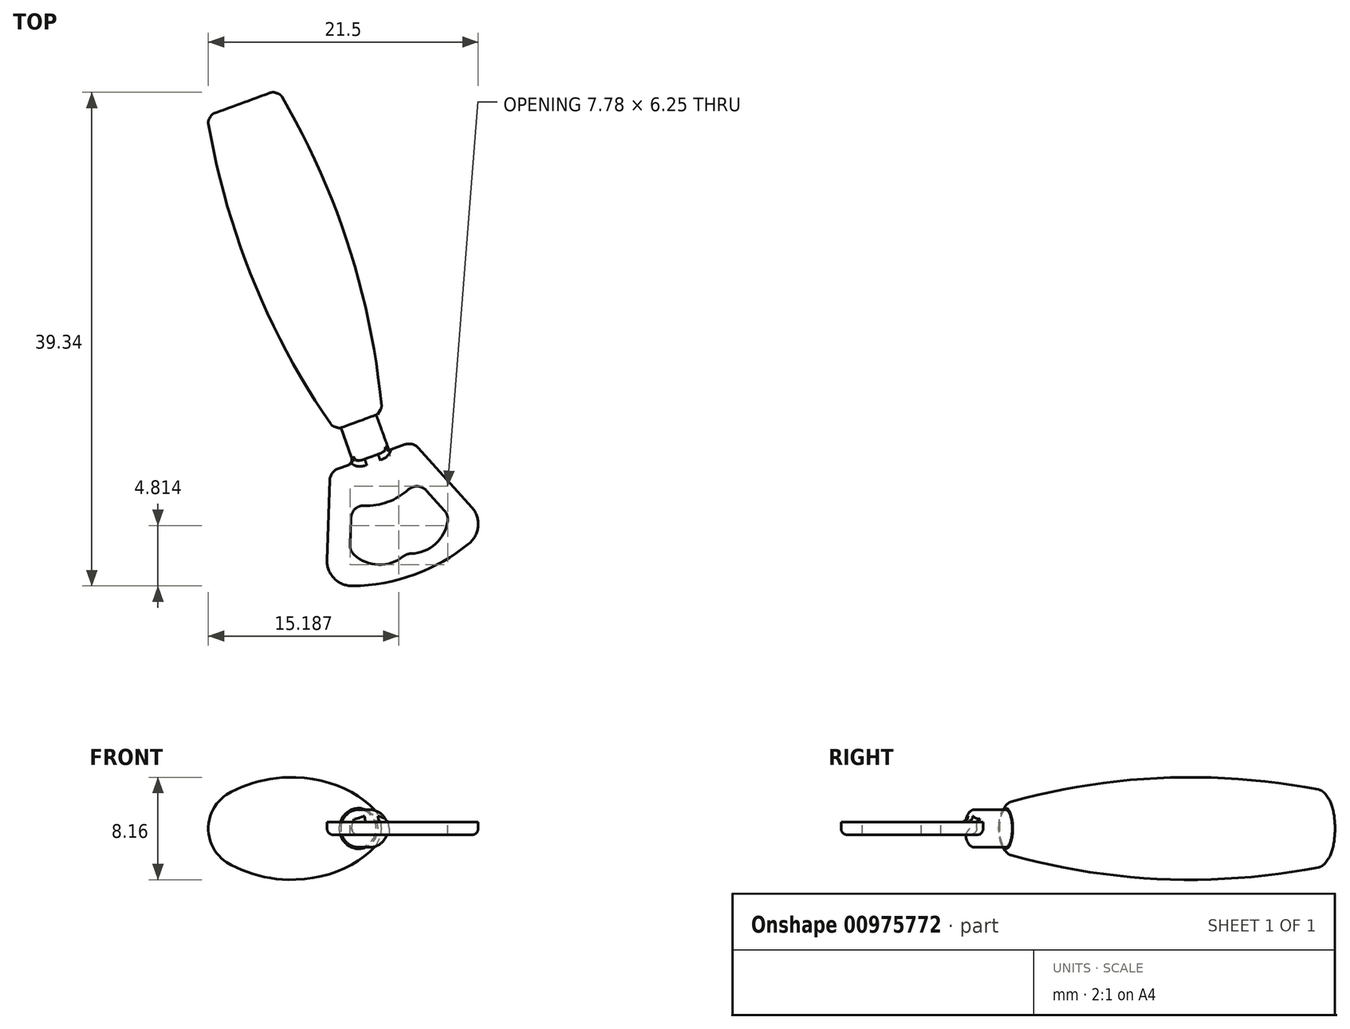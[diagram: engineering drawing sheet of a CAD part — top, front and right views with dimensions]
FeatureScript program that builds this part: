
annotation { "Feature Type Name" : "Feature", "Feature Type Description" : "" }
export const myFeature = defineFeature(function(context is Context, id is Id, definition is map)
    precondition{}
    {
        {
            var Q0;
            Q0=qCreatedBy(makeId("Top.planeOp"),FACE);
            var sketch = newSketch(context, id + "F0", { "sketchPlane" : qUnion([Q0])});
            skLineSegment(sketch, "E0", {"start": v(2.66, 0.97) * mm, "end": v(-2.66, -0.97) * mm});
            skLineSegment(sketch, "E1", {"start": v(-3.31, -1.87) * mm, "end": v(-3.53, -8.23) * mm});
            skArc(sketch, "E2", {"start": v(-1.5, -10.3) * mm, "mid": v(3.42, -9.4) * mm, "end": v(7.78, -6.92) * mm});
            skLineSegment(sketch, "E3", {"start": v(8, -4.03) * mm, "end": v(3.74, 0.7) * mm});
            skLineSegment(sketch, "E4", {"start": v(0, 0) * mm, "end": v(4.2, -11.51) * mm, "construction": true});
            skArc(sketch, "E5", {"start": v(-3.53, -8.23) * mm, "mid": v(-2.97, -9.7) * mm, "end": v(-1.5, -10.3) * mm});
            skPoint(sketch, "E6.visualSharp", {"position": v(-3.29, -1.2) * mm});
            skArc(sketch, "E6.filletArc", {"start": v(-2.66, -0.97) * mm, "mid": v(-3.12, -1.32) * mm, "end": v(-3.31, -1.87) * mm});
            skPoint(sketch, "E7.visualSharp", {"position": v(3.29, 1.2) * mm});
            skArc(sketch, "E7.filletArc", {"start": v(3.74, 0.7) * mm, "mid": v(3.24, 1) * mm, "end": v(2.66, 0.97) * mm});
            skArc(sketch, "E8.filletArc", {"start": v(7.78, -6.92) * mm, "mid": v(8.5, -5.52) * mm, "end": v(8, -4.03) * mm});
            skArc(sketch, "E9", {"start": v(-0.58, -3.9) * mm, "mid": v(1.31, -3.6) * mm, "end": v(2.95, -2.62) * mm});
            skLineSegment(sketch, "E10", {"start": v(-1.62, -4.87) * mm, "end": v(-1.7, -7.05) * mm});
            skArc(sketch, "E11", {"start": v(-1.37, -7.82) * mm, "mid": v(0.57, -8.61) * mm, "end": v(2.55, -7.95) * mm});
            skArc(sketch, "E12", {"start": v(3.16, -7.72) * mm, "mid": v(5.1, -6.96) * mm, "end": v(6.08, -5.11) * mm});
            skLineSegment(sketch, "E13", {"start": v(4.37, -2.7) * mm, "end": v(5.83, -4.31) * mm});
            skPoint(sketch, "E14.visualSharp", {"position": v(2.8, -7.7) * mm});
            skArc(sketch, "E14.filletArc", {"start": v(3.16, -7.72) * mm, "mid": v(2.83, -7.78) * mm, "end": v(2.55, -7.95) * mm});
            skPoint(sketch, "E15.visualSharp", {"position": v(-1.7, -7.46) * mm});
            skArc(sketch, "E15.filletArc", {"start": v(-1.7, -7.05) * mm, "mid": v(-1.62, -7.47) * mm, "end": v(-1.37, -7.82) * mm});
            skPoint(sketch, "E16.visualSharp", {"position": v(6.1, -4.62) * mm});
            skArc(sketch, "E16.filletArc", {"start": v(6.08, -5.11) * mm, "mid": v(6.04, -4.69) * mm, "end": v(5.83, -4.31) * mm});
            skPoint(sketch, "E17.visualSharp", {"position": v(3.63, -1.87) * mm});
            skArc(sketch, "E17.filletArc", {"start": v(4.37, -2.7) * mm, "mid": v(3.68, -2.36) * mm, "end": v(2.95, -2.62) * mm});
            skPoint(sketch, "E18.visualSharp", {"position": v(-1.58, -3.77) * mm});
            skArc(sketch, "E18.filletArc", {"start": v(-0.58, -3.9) * mm, "mid": v(-1.3, -4.17) * mm, "end": v(-1.62, -4.87) * mm});
            skSolve(sketch);
        }
        {
            var Q0;
            Q0=makeQuery(id+"F0.imprint","IMPRINT",FACE,{"disambiguationData":[TD([[makeQuery(id+"F0.imprint","IMPRINT",EDGE,{"derivedFrom":sQuery(id+"F0.wireOp",EDGE,"E0")}),1.0]])]});
            extrude(context, id + "F1", {"entities" : qUnion([Q0]), "endBound" : BoundingType.SYMMETRIC, "oppositeDirection" : true, "depth" : 1 * mm, "offsetDistance" : 25 * mm});
        }
        {
            var Q0;
            Q0=qCreatedBy(makeId("Origin.pointOp"),VERTEX);
            var Q1;
            Q1=makeQuery(id+"F1.opExtrude","CAP_EDGE",EDGE,{"disambiguationData":[OSD([sQuery(id+"F0.wireOp",EDGE,"E0")])],"isStart":true});
            cPlane(context, id + "F2", {"entities" : qUnion([Q0, Q1]), "cplaneType" : CPlaneType.LINE_POINT, "offset" : 25 * mm, "width" : 150 * mm, "height" : 150 * mm});
        }
        {
            var Q0;
            Q0=qCreatedBy(id+"F2.planeOp",FACE);
            var sketch = newSketch(context, id + "F3", { "sketchPlane" : qUnion([Q0])});
            skLineSegment(sketch, "E19.bottom", {"start": v(0, 0) * mm, "end": v(-3, 0) * mm});
            skLineSegment(sketch, "E19.top", {"start": v(0, 1.5) * mm, "end": v(-3, 1.5) * mm});
            skLineSegment(sketch, "E19.left", {"start": v(0, 0) * mm, "end": v(0, 1.5) * mm});
            skLineSegment(sketch, "E19.right", {"start": v(-3, 0) * mm, "end": v(-3, 1.5) * mm});
            skSolve(sketch);
        }
        {
            var Q0;
            Q0=makeQuery(id+"F3.imprint","IMPRINT",FACE,{"disambiguationData":[TD([[makeQuery(id+"F3.imprint","IMPRINT",EDGE,{"derivedFrom":sQuery(id+"F3.wireOp",EDGE,"E19.bottom")}),-1.0]])]});
            var Q1;
            Q1=sQuery(id+"F3.wireOp",EDGE,"E19.bottom");
            revolve(context, id + "F4", {"operationType" : NewBodyOperationType.ADD, "surfaceOperationType" : NewSurfaceOperationType.NEW, "entities" : qUnion([Q0]), "axis" : qUnion([Q1]), "revolveType" : RevolveType.FULL});
        }
        {
            var Q0;
            Q0=qCreatedBy(makeId("Top.planeOp"),FACE);
            var sketch = newSketch(context, id + "F5", { "sketchPlane" : qUnion([Q0])});
            skLineSegment(sketch, "E20", {"start": v(-1.03, 2.82) * mm, "end": v(-2.9, 2.14) * mm});
            skArc(sketch, "E21", {"start": v(-13.08, 27.16) * mm, "mid": v(-9.42, 14.07) * mm, "end": v(-2.9, 2.14) * mm});
            skLineSegment(sketch, "E22", {"start": v(-13.08, 27.16) * mm, "end": v(-10.26, 28.2) * mm});
            skLineSegment(sketch, "E23", {"start": v(-10.26, 28.2) * mm, "end": v(-1.03, 2.82) * mm});
            skSolve(sketch);
        }
        {
            var Q0;
            Q0=makeQuery(id+"F5.imprint","IMPRINT",FACE,{"disambiguationData":[TD([[makeQuery(id+"F5.imprint","IMPRINT",EDGE,{"derivedFrom":sQuery(id+"F5.wireOp",EDGE,"E20")}),-1.0]])]});
            var Q1;
            Q1=sQuery(id+"F5.wireOp",EDGE,"E23");
            revolve(context, id + "F6", {"operationType" : NewBodyOperationType.ADD, "surfaceOperationType" : NewSurfaceOperationType.NEW, "entities" : qUnion([Q0]), "axis" : qUnion([Q1]), "revolveType" : RevolveType.FULL});
        }
        {
            var Q0;
            {var subQ0=sQuery(id+"F3.wireOp",EDGE,"E19.top");Q0=makeQuery(id+"F4.boolean.opBoolean","SPLIT",EDGE,{"disambiguationData":[topologyDisambiguationEdgeConnected([makeQuery(id+"F1.opExtrude","SWEPT_FACE",FACE,{"disambiguationData":[OSD([sQuery(id+"F0.wireOp",EDGE,"E0")])]}),makeQuery(id+"F4.opRevolve","SWEPT_FACE",FACE,{"disambiguationData":[OSD([subQ0])]})]),OD(1.0)],"derivedFrom":makeQuery(id+"F4.opRevolve","SWEPT_EDGE",EDGE,{"disambiguationData":[OSD([subQ0,sQuery(id+"F3.wireOp",EDGE,"E19.left")])]})});}
            var Q1;
            {var subQ0=sQuery(id+"F3.wireOp",EDGE,"E19.top");Q1=makeQuery(id+"F4.boolean.opBoolean","SPLIT",EDGE,{"disambiguationData":[topologyDisambiguationEdgeConnected([makeQuery(id+"F1.opExtrude","SWEPT_FACE",FACE,{"disambiguationData":[OSD([sQuery(id+"F0.wireOp",EDGE,"E0")])]}),makeQuery(id+"F4.opRevolve","SWEPT_FACE",FACE,{"disambiguationData":[OSD([subQ0])]})]),OD(0.0)],"derivedFrom":makeQuery(id+"F4.opRevolve","SWEPT_EDGE",EDGE,{"disambiguationData":[OSD([subQ0,sQuery(id+"F3.wireOp",EDGE,"E19.left")])]})});}
            fillet(context, id + "F7", {"entities" : qUnion([Q0, Q1]), "radius" : 0.5 * mm, "tangentPropagation" : true, "allowEdgeOverflow" : false});
        }
        {
            var Q0;
            {var subQ0=sQuery(id+"F0.wireOp",EDGE,"E0");var subQ1=sQuery(id+"F3.wireOp",EDGE,"E19.left");var subQ2=makeQuery(id+"F4.opRevolve","SWEPT_FACE",FACE,{"disambiguationData":[OSD([subQ1])]});var subQ3=sQuery(id+"F3.wireOp",EDGE,"E19.top");var subQ4=makeQuery(id+"F4.opRevolve","SWEPT_FACE",FACE,{"disambiguationData":[OSD([subQ3])]});Q0=makeQuery(id+"F4.boolean.opBoolean","SPLIT",EDGE,{"disambiguationData":[topologyDisambiguationEdgeConnected([subQ4,subQ2]),TD([makeQuery(id+"F1.opExtrude","CAP_FACE",FACE,{"disambiguationData":[OSD([subQ0,sQuery(id+"F0.wireOp",EDGE,"E1"),sQuery(id+"F0.wireOp",EDGE,"E2"),sQuery(id+"F0.wireOp",EDGE,"E3"),sQuery(id+"F0.wireOp",EDGE,"E5"),sQuery(id+"F0.wireOp",EDGE,"E6.filletArc"),sQuery(id+"F0.wireOp",EDGE,"E7.filletArc"),sQuery(id+"F0.wireOp",EDGE,"E8.filletArc"),sQuery(id+"F0.wireOp",EDGE,"E9"),sQuery(id+"F0.wireOp",EDGE,"E10"),sQuery(id+"F0.wireOp",EDGE,"E11"),sQuery(id+"F0.wireOp",EDGE,"E12"),sQuery(id+"F0.wireOp",EDGE,"E13"),sQuery(id+"F0.wireOp",EDGE,"E14.filletArc"),sQuery(id+"F0.wireOp",EDGE,"E15.filletArc"),sQuery(id+"F0.wireOp",EDGE,"E16.filletArc"),sQuery(id+"F0.wireOp",EDGE,"E17.filletArc"),sQuery(id+"F0.wireOp",EDGE,"E18.filletArc")])],"isStart":true})])],"derivedFrom":makeQuery(id+"F4.opRevolve","SWEPT_EDGE",EDGE,{"disambiguationData":[OSD([subQ3,subQ1])]})});}
            var Q1;
            {var subQ0=sQuery(id+"F0.wireOp",EDGE,"E0");var subQ1=sQuery(id+"F3.wireOp",EDGE,"E19.left");var subQ2=makeQuery(id+"F4.opRevolve","SWEPT_FACE",FACE,{"disambiguationData":[OSD([subQ1])]});var subQ3=sQuery(id+"F3.wireOp",EDGE,"E19.top");var subQ4=makeQuery(id+"F4.opRevolve","SWEPT_FACE",FACE,{"disambiguationData":[OSD([subQ3])]});Q1=makeQuery(id+"F4.boolean.opBoolean","SPLIT",EDGE,{"disambiguationData":[topologyDisambiguationEdgeConnected([subQ4,subQ2]),TD([makeQuery(id+"F1.opExtrude","CAP_FACE",FACE,{"disambiguationData":[OSD([subQ0,sQuery(id+"F0.wireOp",EDGE,"E1"),sQuery(id+"F0.wireOp",EDGE,"E2"),sQuery(id+"F0.wireOp",EDGE,"E3"),sQuery(id+"F0.wireOp",EDGE,"E5"),sQuery(id+"F0.wireOp",EDGE,"E6.filletArc"),sQuery(id+"F0.wireOp",EDGE,"E7.filletArc"),sQuery(id+"F0.wireOp",EDGE,"E8.filletArc"),sQuery(id+"F0.wireOp",EDGE,"E9"),sQuery(id+"F0.wireOp",EDGE,"E10"),sQuery(id+"F0.wireOp",EDGE,"E11"),sQuery(id+"F0.wireOp",EDGE,"E12"),sQuery(id+"F0.wireOp",EDGE,"E13"),sQuery(id+"F0.wireOp",EDGE,"E14.filletArc"),sQuery(id+"F0.wireOp",EDGE,"E15.filletArc"),sQuery(id+"F0.wireOp",EDGE,"E16.filletArc"),sQuery(id+"F0.wireOp",EDGE,"E17.filletArc"),sQuery(id+"F0.wireOp",EDGE,"E18.filletArc")])],"isStart":false})])],"derivedFrom":makeQuery(id+"F4.opRevolve","SWEPT_EDGE",EDGE,{"disambiguationData":[OSD([subQ3,subQ1])]})});}
            fillet(context, id + "F8", {"entities" : qUnion([Q0, Q1]), "radius" : 0.35 * mm, "tangentPropagation" : true, "allowEdgeOverflow" : false});
        }
        {
            var Q0;
            {var subQ0=sQuery(id+"F0.wireOp",EDGE,"E0");Q0=makeQuery(id+"F4.boolean.opBoolean","SPLIT",EDGE,{"disambiguationData":[topologyDisambiguationEdgeConnected([makeQuery(id+"F1.opExtrude","CAP_FACE",FACE,{"disambiguationData":[OSD([subQ0,sQuery(id+"F0.wireOp",EDGE,"E1"),sQuery(id+"F0.wireOp",EDGE,"E2"),sQuery(id+"F0.wireOp",EDGE,"E3"),sQuery(id+"F0.wireOp",EDGE,"E5"),sQuery(id+"F0.wireOp",EDGE,"E6.filletArc"),sQuery(id+"F0.wireOp",EDGE,"E7.filletArc"),sQuery(id+"F0.wireOp",EDGE,"E8.filletArc"),sQuery(id+"F0.wireOp",EDGE,"E9"),sQuery(id+"F0.wireOp",EDGE,"E10"),sQuery(id+"F0.wireOp",EDGE,"E11"),sQuery(id+"F0.wireOp",EDGE,"E12"),sQuery(id+"F0.wireOp",EDGE,"E13"),sQuery(id+"F0.wireOp",EDGE,"E14.filletArc"),sQuery(id+"F0.wireOp",EDGE,"E15.filletArc"),sQuery(id+"F0.wireOp",EDGE,"E16.filletArc"),sQuery(id+"F0.wireOp",EDGE,"E17.filletArc"),sQuery(id+"F0.wireOp",EDGE,"E18.filletArc")])],"isStart":true}),makeQuery(id+"F4.opRevolve","SWEPT_FACE",FACE,{"disambiguationData":[OSD([sQuery(id+"F3.wireOp",EDGE,"E19.left")])]})])],"derivedFrom":makeQuery(id+"F1.opExtrude","CAP_EDGE",EDGE,{"disambiguationData":[OSD([subQ0])],"isStart":true})});}
            var Q1;
            {var subQ0=sQuery(id+"F0.wireOp",EDGE,"E0");Q1=makeQuery(id+"F4.boolean.opBoolean","SPLIT",EDGE,{"disambiguationData":[topologyDisambiguationEdgeConnected([makeQuery(id+"F1.opExtrude","CAP_FACE",FACE,{"disambiguationData":[OSD([subQ0,sQuery(id+"F0.wireOp",EDGE,"E1"),sQuery(id+"F0.wireOp",EDGE,"E2"),sQuery(id+"F0.wireOp",EDGE,"E3"),sQuery(id+"F0.wireOp",EDGE,"E5"),sQuery(id+"F0.wireOp",EDGE,"E6.filletArc"),sQuery(id+"F0.wireOp",EDGE,"E7.filletArc"),sQuery(id+"F0.wireOp",EDGE,"E8.filletArc"),sQuery(id+"F0.wireOp",EDGE,"E9"),sQuery(id+"F0.wireOp",EDGE,"E10"),sQuery(id+"F0.wireOp",EDGE,"E11"),sQuery(id+"F0.wireOp",EDGE,"E12"),sQuery(id+"F0.wireOp",EDGE,"E13"),sQuery(id+"F0.wireOp",EDGE,"E14.filletArc"),sQuery(id+"F0.wireOp",EDGE,"E15.filletArc"),sQuery(id+"F0.wireOp",EDGE,"E16.filletArc"),sQuery(id+"F0.wireOp",EDGE,"E17.filletArc"),sQuery(id+"F0.wireOp",EDGE,"E18.filletArc")])],"isStart":false}),makeQuery(id+"F4.opRevolve","SWEPT_FACE",FACE,{"disambiguationData":[OSD([sQuery(id+"F3.wireOp",EDGE,"E19.left")])]})])],"derivedFrom":makeQuery(id+"F1.opExtrude","CAP_EDGE",EDGE,{"disambiguationData":[OSD([subQ0])],"isStart":false})});}
            fillet(context, id + "F9", {"entities" : qUnion([Q0, Q1]), "radius" : 0.5 * mm, "tangentPropagation" : true, "allowEdgeOverflow" : false});
        }
        {
            var Q0;
            Q0=makeQuery(id+"F6.opRevolve","SWEPT_EDGE",EDGE,{"disambiguationData":[OSD([sQuery(id+"F5.wireOp",EDGE,"E20"),sQuery(id+"F5.wireOp",EDGE,"E21")])]});
            var Q1;
            Q1=makeQuery(id+"F6.opRevolve","SWEPT_EDGE",EDGE,{"disambiguationData":[OSD([sQuery(id+"F5.wireOp",EDGE,"E21"),sQuery(id+"F5.wireOp",EDGE,"E22")])]});
            chamfer(context, id + "F10", {"entities" : qUnion([Q0, Q1]), "width" : 0.5 * mm, "tangentPropagation" : true});
        }
        {
            var Q0;
            Q0=makeQuery(id+"F10.opChamfer","BLEND_EDGE",EDGE,{"blendedFrom":[makeQuery(id+"F6.opRevolve","SWEPT_EDGE",EDGE,{"disambiguationData":[OSD([sQuery(id+"F5.wireOp",EDGE,"E20"),sQuery(id+"F5.wireOp",EDGE,"E21")])]}),makeQuery(id+"F4.opRevolve","SWEPT_FACE",FACE,{"disambiguationData":[OSD([sQuery(id+"F3.wireOp",EDGE,"E19.top")])]})],"blendedInto":[makeQuery(id+"F4.opRevolve","SWEPT_FACE",FACE,{"disambiguationData":[OSD([sQuery(id+"F3.wireOp",EDGE,"E19.top")])]})]});
            var Q1;
            {var subQ0=sQuery(id+"F5.wireOp",EDGE,"E21");Q1=makeQuery(id+"F10.opChamfer","BLEND_EDGE",EDGE,{"blendedFrom":[makeQuery(id+"F6.opRevolve","SWEPT_EDGE",EDGE,{"disambiguationData":[OSD([sQuery(id+"F5.wireOp",EDGE,"E20"),subQ0])]}),makeQuery(id+"F6.opRevolve","SWEPT_FACE",FACE,{"disambiguationData":[OSD([subQ0])]})],"blendedInto":[makeQuery(id+"F6.opRevolve","SWEPT_FACE",FACE,{"disambiguationData":[OSD([subQ0])]})]});}
            var Q2;
            {var subQ0=sQuery(id+"F5.wireOp",EDGE,"E21");Q2=makeQuery(id+"F10.opChamfer","BLEND_EDGE",EDGE,{"blendedFrom":[makeQuery(id+"F6.opRevolve","SWEPT_EDGE",EDGE,{"disambiguationData":[OSD([subQ0,sQuery(id+"F5.wireOp",EDGE,"E22")])]}),makeQuery(id+"F6.opRevolve","SWEPT_FACE",FACE,{"disambiguationData":[OSD([subQ0])]})],"blendedInto":[makeQuery(id+"F6.opRevolve","SWEPT_FACE",FACE,{"disambiguationData":[OSD([subQ0])]})]});}
            var Q3;
            {var subQ0=sQuery(id+"F5.wireOp",EDGE,"E22");Q3=makeQuery(id+"F10.opChamfer","BLEND_EDGE",EDGE,{"blendedFrom":[makeQuery(id+"F6.opRevolve","SWEPT_EDGE",EDGE,{"disambiguationData":[OSD([sQuery(id+"F5.wireOp",EDGE,"E21"),subQ0])]}),makeQuery(id+"F6.opRevolve","SWEPT_FACE",FACE,{"disambiguationData":[OSD([subQ0])]})],"blendedInto":[makeQuery(id+"F6.opRevolve","SWEPT_FACE",FACE,{"disambiguationData":[OSD([subQ0])]})]});}
            fillet(context, id + "F11", {"entities" : qUnion([Q0, Q1, Q2, Q3]), "radius" : 0.5 * mm, "tangentPropagation" : true, "allowEdgeOverflow" : false});
        }
    });
